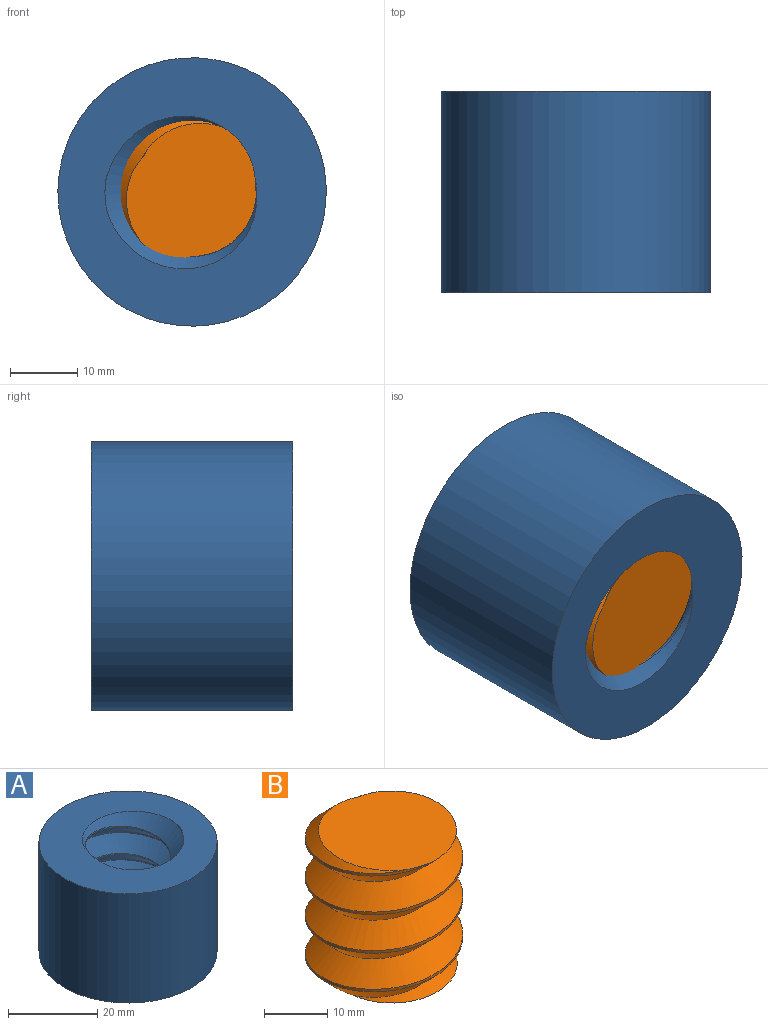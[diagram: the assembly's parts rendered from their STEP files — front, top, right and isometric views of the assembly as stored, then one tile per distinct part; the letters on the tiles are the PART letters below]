
ASSEMBLY  parts=2 mates=1
PART A: 7 faces, bbox 42.4x42.4x40.7 mm
  f0: bspline ~37.3x26mm, area 1360mm2, adj f2,f4,f5,f6
  f1: bspline ~38.24x26mm, area 1360.1mm2, adj f2,f4,f5,f6
  f2: cylinder r=13mm len=30mm, axis (0,0,-1), area 117.8mm2, adj f0,f1,f4,f5
  f3: cylinder r=20mm len=40mm, axis (0,0,-1), area 3769.9mm2, adj f4,f5
  f4: plane 42.43x42.43mm, normal (0,0,1), area 850.4mm2, adj f0,f1,f2,f3,f6
  f5: plane 42.43x42.43mm, normal (0,0,-1), area 850.4mm2, adj f0,f1,f2,f3,f6
  f6: bspline ~30.87x19.27mm, area 95.7mm2, adj f0,f1,f4,f5
PART B: 5 faces, bbox 27.6x27.6x38.2 mm
  f0: cylinder r=12.5mm len=27.5mm, axis (0,0,-1), area 143.8mm2, adj f1,f2,f3,f4
  f1: bspline ~35.38x25mm, area 1229.9mm2, adj f0,f2,f3,f4
  f2: bspline ~35.38x25mm, area 1228.7mm2, adj f0,f1,f3,f4
  f3: plane 24.48x24.43mm, normal (0,0,-1), area 374.6mm2, adj f0,f1,f2
  f4: plane 24.48x24.48mm, normal (0,0,1), area 374.6mm2, adj f0,f1,f2
PLACE A rot(axis=(0.08,0.7,-0.7),170.4deg) t=(38.89,0.8,9.36)mm
PLACE B rot(axis=(0.69,-0.51,0.51),111.1deg) t=(-11.24,0.3,-38.39)mm
MATE cylindrical B.f0 <-> A.f3  axis (0,1,0) through (0,0,0)mm
